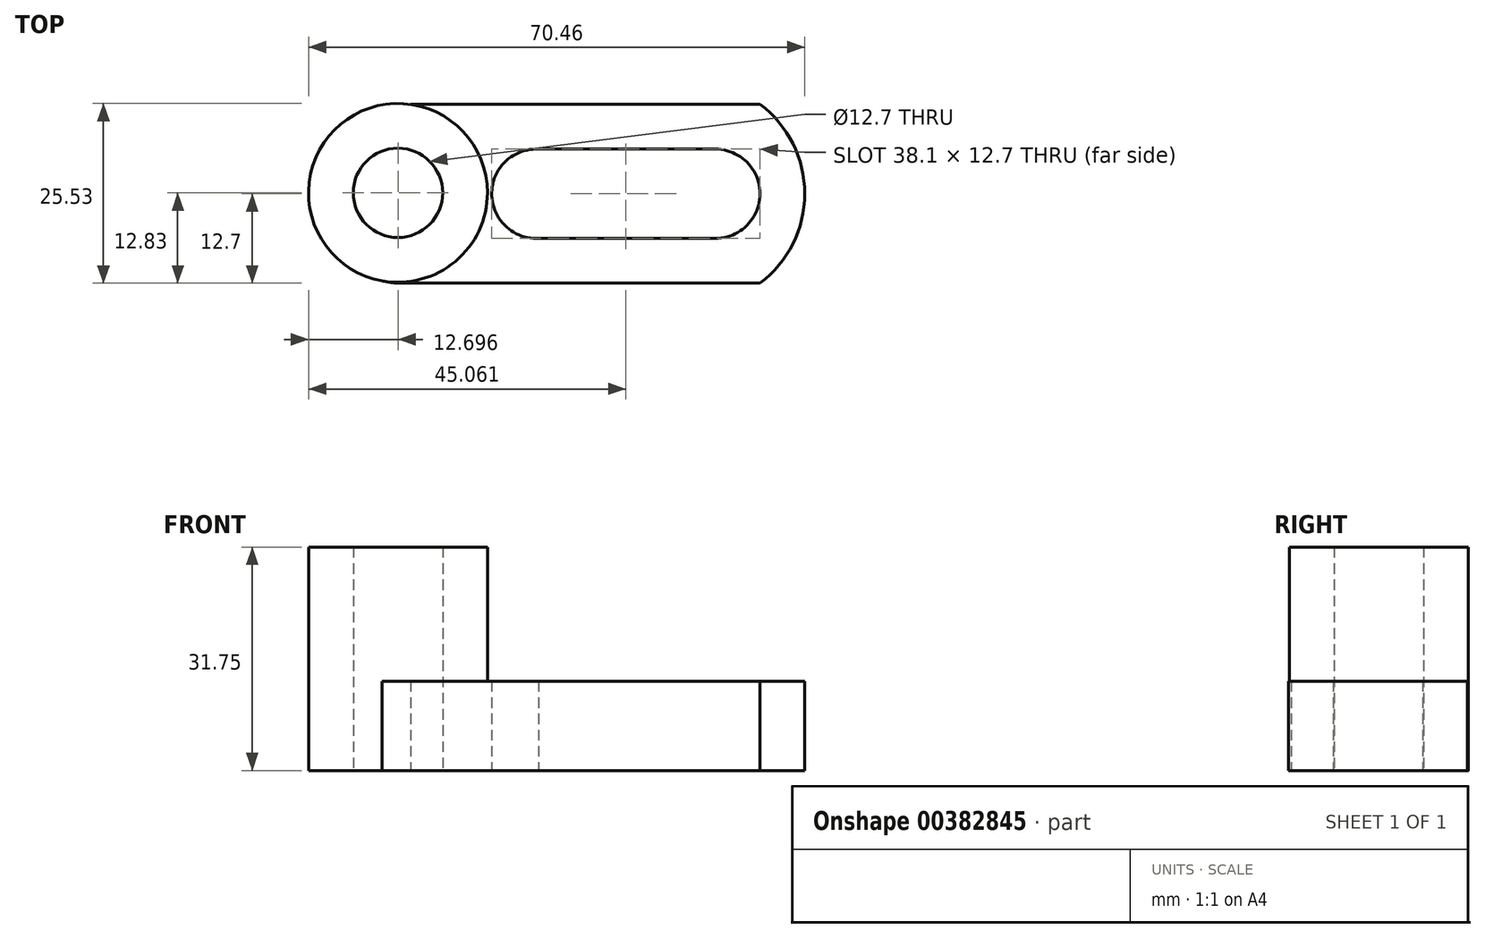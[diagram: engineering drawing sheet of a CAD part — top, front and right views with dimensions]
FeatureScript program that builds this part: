
annotation { "Feature Type Name" : "Feature", "Feature Type Description" : "" }
export const myFeature = defineFeature(function(context is Context, id is Id, definition is map)
    precondition{}
    {
        {
            var Q0;
            Q0=qCreatedBy(makeId("Front.planeOp"),FACE);
            var sketch = newSketch(context, id + "F0", { "sketchPlane" : qUnion([Q0])});
            skLineSegment(sketch, "E0", {"start": v(0, 0) * mm, "end": v(69.85, 0) * mm});
            skLineSegment(sketch, "E1", {"start": v(69.85, 0) * mm, "end": v(69.85, 12.7) * mm});
            skLineSegment(sketch, "E2", {"start": v(69.85, 12.7) * mm, "end": v(0, 12.7) * mm});
            skLineSegment(sketch, "E3", {"start": v(0, 12.7) * mm, "end": v(0, 0) * mm});
            skSolve(sketch);
        }
        {
            var Q0;
            Q0 = qSketchRegion(id + "F0", true);
            extrude(context, id + "F1", {"entities" : qUnion([Q0]), "depth" : 25.4 * mm});
        }
        {
            var Q0;
            Q0=qCreatedBy(makeId("Top.planeOp"),FACE);
            var sketch = newSketch(context, id + "F2", { "sketchPlane" : qUnion([Q0])});
            skCircle(sketch, "E4", {"center": v(57.15, -12.7) * mm, "radius": 6.35 * mm});
            skCircle(sketch, "E5", {"center": v(31.75, -12.7) * mm, "radius": 6.35 * mm});
            skLineSegment(sketch, "E6", {"start": v(31.42, -6.36) * mm, "end": v(57.15, -6.35) * mm});
            skLineSegment(sketch, "E7", {"start": v(57.15, -6.35) * mm, "end": v(57.15, -19.05) * mm});
            skLineSegment(sketch, "E8", {"start": v(57.15, -19.05) * mm, "end": v(31.75, -19.05) * mm});
            skSolve(sketch);
        }
        {
            var Q0;
            Q0 = qSketchRegion(id + "F2", true);
            extrude(context, id + "F3", {"entities" : qUnion([Q0]), "operationType" : NewBodyOperationType.REMOVE, "depth" : 25.4 * mm});
        }
        {
            var Q0;
            Q0=qCreatedBy(makeId("Top.planeOp"),FACE);
            var sketch = newSketch(context, id + "F4", { "sketchPlane" : qUnion([Q0])});
            skArc(sketch, "E9", {"start": v(63.5, -25.4) * mm, "mid": v(69.85, -12.7) * mm, "end": v(63.5, 0) * mm});
            skLineSegment(sketch, "E10", {"start": v(63.5, 0) * mm, "end": v(69.85, 0) * mm});
            skLineSegment(sketch, "E11", {"start": v(69.85, 0) * mm, "end": v(69.85, -25.4) * mm});
            skLineSegment(sketch, "E12", {"start": v(69.85, -25.4) * mm, "end": v(63.5, -25.4) * mm});
            skSolve(sketch);
        }
        {
            var Q0;
            Q0 = qSketchRegion(id + "F4", true);
            extrude(context, id + "F5", {"entities" : qUnion([Q0]), "operationType" : NewBodyOperationType.REMOVE, "depth" : 25.4 * mm});
        }
        {
            var Q0;
            Q0=qCreatedBy(makeId("Top.planeOp"),FACE);
            var sketch = newSketch(context, id + "F6", { "sketchPlane" : qUnion([Q0])});
            skArc(sketch, "E13", {"start": v(11.6, 0) * mm, "mid": v(0.01, -13.22) * mm, "end": v(12.69, -25.4) * mm});
            skLineSegment(sketch, "E14", {"start": v(11.6, 0) * mm, "end": v(0, 0) * mm});
            skLineSegment(sketch, "E15", {"start": v(0, 0) * mm, "end": v(0, -25.4) * mm});
            skLineSegment(sketch, "E16", {"start": v(0, -25.4) * mm, "end": v(12.69, -25.4) * mm});
            skSolve(sketch);
        }
        {
            var Q0;
            Q0 = qSketchRegion(id + "F6", true);
            extrude(context, id + "F7", {"entities" : qUnion([Q0]), "operationType" : NewBodyOperationType.REMOVE, "depth" : 25.4 * mm});
        }
        {
            var Q0;
            Q0=qCreatedBy(makeId("Top.planeOp"),FACE);
            var sketch = newSketch(context, id + "F8", { "sketchPlane" : qUnion([Q0])});
            skCircle(sketch, "E17", {"center": v(12.09, -12.57) * mm, "radius": 12.7 * mm});
            skSolve(sketch);
        }
        {
            var Q0;
            Q0 = qSketchRegion(id + "F8", true);
            extrude(context, id + "F9", {"entities" : qUnion([Q0]), "operationType" : NewBodyOperationType.ADD, "depth" : 31.75 * mm});
        }
        {
            var Q0;
            Q0=qCreatedBy(makeId("Top.planeOp"),FACE);
            var sketch = newSketch(context, id + "F10", { "sketchPlane" : qUnion([Q0])});
            skCircle(sketch, "E18", {"center": v(12.09, -12.57) * mm, "radius": 6.35 * mm});
            skSolve(sketch);
        }
        {
            var Q0;
            Q0 = qSketchRegion(id + "F10", true);
            extrude(context, id + "F11", {"entities" : qUnion([Q0]), "operationType" : NewBodyOperationType.REMOVE, "depth" : 38.1 * mm});
        }
    });
